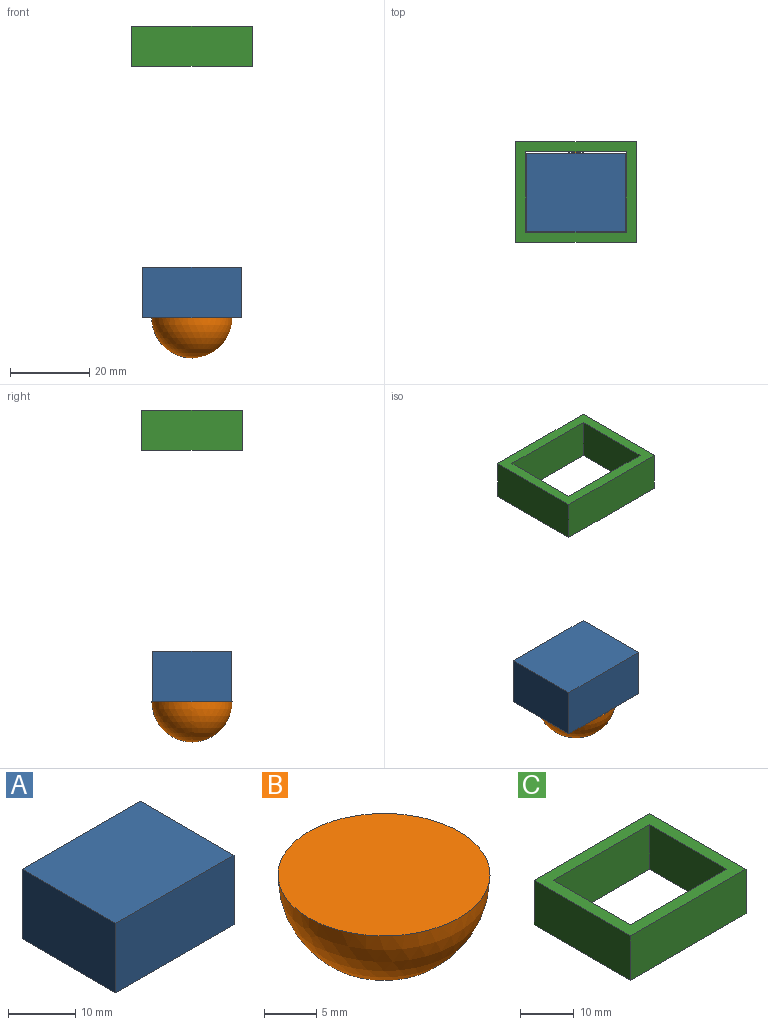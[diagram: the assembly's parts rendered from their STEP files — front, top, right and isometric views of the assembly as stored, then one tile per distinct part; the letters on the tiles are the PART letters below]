
ASSEMBLY  parts=3 mates=1
PART A: 6 faces, bbox 24.9x19.8x12.7 mm
  f0: plane 24.89x12.7mm, normal (0,1,0), area 316.1mm2, adj f1,f3,f4,f5
  f1: plane 19.81x12.7mm, normal (-1,0,0), area 251.6mm2, adj f0,f2,f4,f5
  f2: plane 24.89x12.7mm, normal (0,-1,0), area 316.1mm2, adj f1,f3,f4,f5
  f3: plane 19.81x12.7mm, normal (1,0,0), area 251.6mm2, adj f0,f2,f4,f5
  f4: plane 24.89x19.81mm, normal (0,0,1), area 493.2mm2, adj f0,f1,f2,f3
  f5: plane 24.89x19.81mm, normal (0,0,-1), area 493.2mm2, adj f0,f1,f2,f3
PART B: 2 faces, bbox 20.3x20.3x10.2 mm
  f0: sphere r=10.16mm, area 648.6mm2, adj f1
  f1: plane 20.32x20.32mm, normal (0,0,1), area 324.3mm2, adj f0
PART C: 10 faces, bbox 30.5x25.4x10.2 mm
  f0: plane 30.48x10.16mm, normal (0,1,0), area 309.7mm2, adj f1,f7,f8,f9
  f1: plane 25.4x10.16mm, normal (-1,0,0), area 258.1mm2, adj f0,f2,f8,f9
  f2: plane 30.48x10.16mm, normal (0,-1,0), area 309.7mm2, adj f1,f7,f8,f9
  f3: plane 20.32x10.16mm, normal (1,0,0), area 206.5mm2, adj f4,f6,f8,f9
  f4: plane 25.4x10.16mm, normal (0,-1,0), area 258.1mm2, adj f3,f5,f8,f9
  f5: plane 20.32x10.16mm, normal (-1,0,0), area 206.5mm2, adj f4,f6,f8,f9
  f6: plane 25.4x10.16mm, normal (0,1,0), area 258.1mm2, adj f3,f5,f8,f9
  f7: plane 25.4x10.16mm, normal (1,0,0), area 258.1mm2, adj f0,f2,f8,f9
  f8: plane 30.48x25.4mm, normal (0,0,1), area 258.1mm2, adj f0,f1,f2,f3,f4,f5,f6,f7
  f9: plane 30.48x25.4mm, normal (0,0,-1), area 258.1mm2, adj f0,f1,f2,f3,f4,f5,f6,f7
PLACE A t=(-51.43,-21.89,-72.74)mm
PLACE B t=(-51.43,-21.89,-79.09)mm
PLACE C t=(-51.43,-21.89,-10.51)mm
MATE fastened B.f1 <-> A.f5  axis (0,0,1) through (-51.43,-21.89,-79.09)mm
